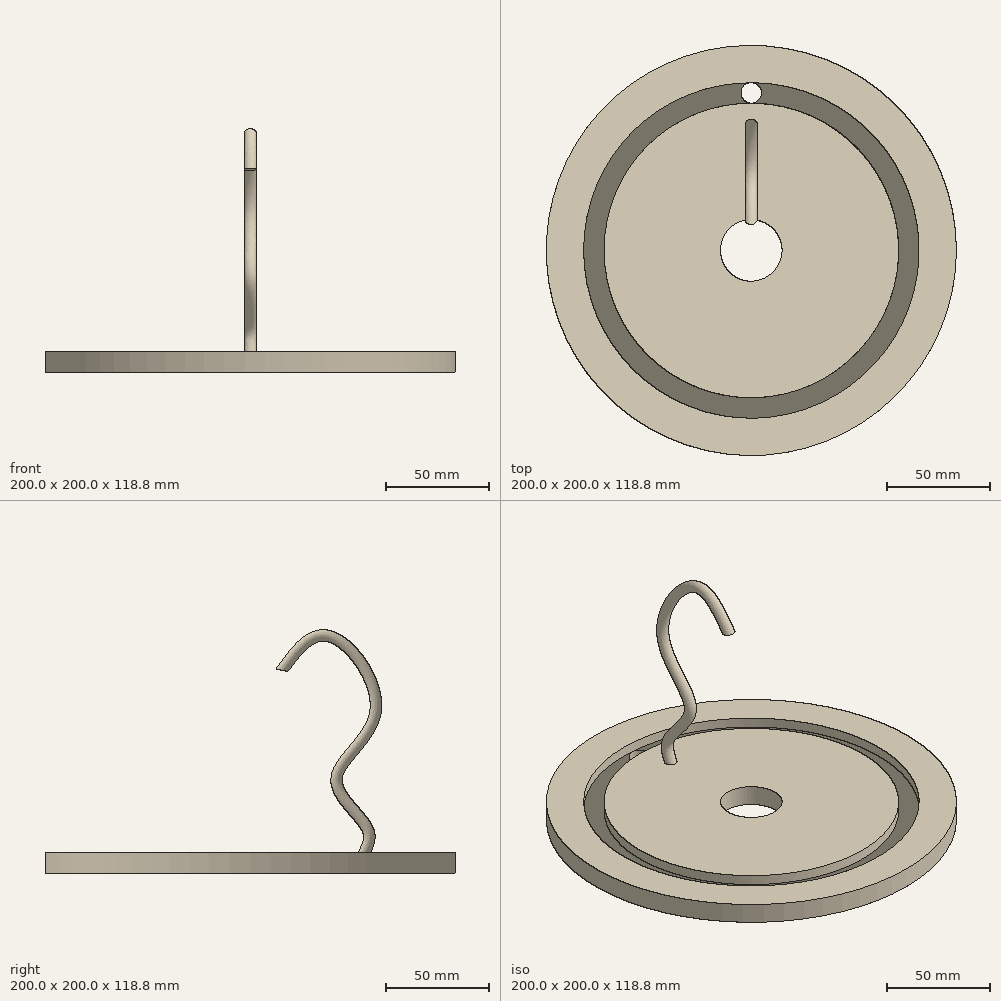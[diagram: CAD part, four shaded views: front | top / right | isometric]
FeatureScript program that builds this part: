
annotation { "Feature Type Name" : "Feature", "Feature Type Description" : "" }
export const myFeature = defineFeature(function(context is Context, id is Id, definition is map)
    precondition{}
    {
        {
            var Q0;
            Q0=qCreatedBy(makeId("Top.planeOp"),FACE);
            var sketch = newSketch(context, id + "F0", { "sketchPlane" : qUnion([Q0])});
            skCircle(sketch, "E0", {"center": v(0, 0) * mm, "radius": 100 * mm});
            skCircle(sketch, "E1", {"center": v(0, 0) * mm, "radius": 15 * mm});
            skSolve(sketch);
        }
        {
            var Q0;
            Q0 = qSketchRegion(id + "F0", true);
            extrude(context, id + "F1", {"entities" : qUnion([Q0]), "depth" : 10 * mm});
        }
        {
            var Q0;
            Q0=makeQuery(id+"F1.opExtrude","CAP_FACE",FACE,{"disambiguationData":[OSD([sQuery(id+"F0.wireOp",EDGE,"E0"),sQuery(id+"F0.wireOp",EDGE,"E1")])],"isStart":false});
            var sketch = newSketch(context, id + "F2", { "sketchPlane" : qUnion([Q0])});
            skCircle(sketch, "E2.0", {"center": v(0, 0) * mm, "radius": 100 * mm, "construction": true});
            skLineSegment(sketch, "E3", {"start": v(0, 0) * mm, "end": v(0, 100) * mm, "construction": true});
            skCircle(sketch, "E4", {"center": v(0, 76.82) * mm, "radius": 5 * mm});
            skSolve(sketch);
        }
        {
            var Q0;
            Q0 = qSketchRegion(id + "F2", true);
            extrude(context, id + "F3", {"entities" : qUnion([Q0]), "operationType" : NewBodyOperationType.REMOVE, "endBound" : BoundingType.THROUGH_ALL, "oppositeDirection" : true, "depth" : 25 * mm});
        }
        {
            var Q0;
            Q0=qCreatedBy(makeId("Right.planeOp"),FACE);
            var sketch = newSketch(context, id + "F4", { "sketchPlane" : qUnion([Q0])});
            skLineSegment(sketch, "E5", {"start": v(71.82, 10) * mm, "end": v(71.82, 0) * mm, "construction": true});
            skLineSegment(sketch, "E6", {"start": v(81.82, 0) * mm, "end": v(81.82, 10) * mm, "construction": true});
            skLineSegment(sketch, "E7.bottom", {"start": v(81.82, 10) * mm, "end": v(71.82, 10) * mm});
            skLineSegment(sketch, "E7.top", {"start": v(81.82, 5) * mm, "end": v(71.82, 5) * mm});
            skLineSegment(sketch, "E7.left", {"start": v(81.82, 10) * mm, "end": v(81.82, 5) * mm});
            skLineSegment(sketch, "E7.right", {"start": v(71.82, 10) * mm, "end": v(71.82, 5) * mm});
            skSolve(sketch);
        }
        {
            var Q0;
            Q0 = qSketchRegion(id + "F4", true);
            var Q1;
            Q1=makeQuery(id+"F1.opExtrude","SWEPT_FACE",FACE,{"disambiguationData":[OSD([sQuery(id+"F0.wireOp",EDGE,"E0")])]});
            revolve(context, id + "F5", {"operationType" : NewBodyOperationType.REMOVE, "entities" : qUnion([Q0]), "axis" : qUnion([Q1]), "revolveType" : RevolveType.FULL, "oppositeDirection" : true});
        }
        {
            var Q0;
            Q0=qCreatedBy(makeId("Right.planeOp"),FACE);
            var sketch = newSketch(context, id + "F6", { "sketchPlane" : qUnion([Q0])});
            skLineSegment(sketch, "E8", {"start": v(-15, 10) * mm, "end": v(-71.82, 10) * mm, "construction": true});
            skLineSegment(sketch, "E9", {"start": v(71.82, 10) * mm, "end": v(15, 10) * mm, "construction": true});
            skFitSpline(sketch, "E10", {"points": [v(55.67, 10) * mm, v(56.98, 21.6) * mm, v(42.05, 45.4) * mm, v(60.9, 78.44) * mm, v(37.92, 115.62) * mm, v(15.51, 98.93) * mm], "startDerivative": vector(39.03, 84.94) * mm, "endDerivative": vector(-103.17, -141.35) * mm});
            skSolve(sketch);
        }
        {
            var Q0;
            {var subQ0=sQuery(id+"F0.wireOp",EDGE,"E1");Q0=makeQuery(id+"F5.boolean.opBoolean","SPLIT",FACE,{"disambiguationData":[TD([makeQuery(id+"F1.opExtrude","SWEPT_FACE",FACE,{"disambiguationData":[OSD([subQ0])]})])],"derivedFrom":makeQuery(id+"F1.opExtrude","CAP_FACE",FACE,{"disambiguationData":[OSD([sQuery(id+"F0.wireOp",EDGE,"E0"),subQ0])],"isStart":false})});}
            var sketch = newSketch(context, id + "F7", { "sketchPlane" : qUnion([Q0])});
            skCircle(sketch, "E11", {"center": v(0, 55.67) * mm, "radius": 3.1 * mm});
            skSolve(sketch);
        }
        {
            var Q0;
            Q0=makeQuery(id+"F7.imprint","IMPRINT",FACE,{"disambiguationData":[TD([[makeQuery(id+"F7.imprint","IMPRINT",EDGE,{"derivedFrom":sQuery(id+"F7.wireOp",EDGE,"E11")}),1.0]])]});
            var Q1;
            Q1 = qConstructionFilter(qBodyType(qCreatedBy(id + "F7" ,EDGE), BodyType.WIRE), ConstructionObject.NO);
            var Q2;
            Q2=sQuery(id+"F6.wireOp",EDGE,"E10");
            sweep(context, id + "F8", {"operationType" : NewBodyOperationType.ADD, "profiles" : qUnion([Q0]), "surfaceProfiles" : qUnion([Q1]), "path" : qUnion([Q2])});
        }
    });
